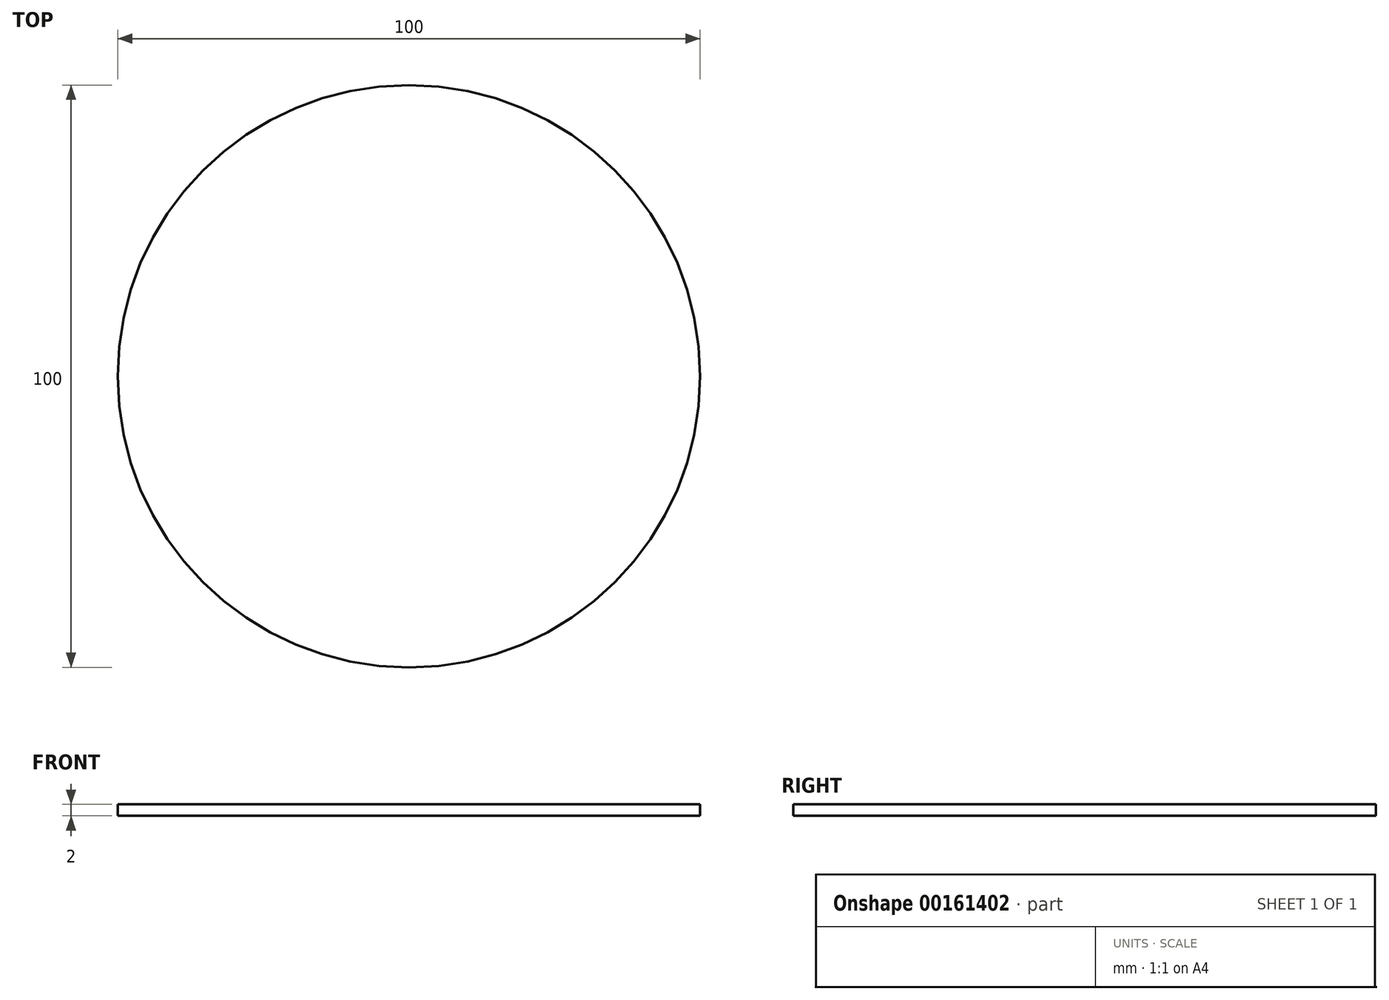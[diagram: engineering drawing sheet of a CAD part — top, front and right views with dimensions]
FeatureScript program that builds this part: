
annotation { "Feature Type Name" : "Feature", "Feature Type Description" : "" }
export const myFeature = defineFeature(function(context is Context, id is Id, definition is map)
    precondition{}
    {
        {
            var Q0;
            Q0=qCreatedBy(makeId("Top.planeOp"),FACE);
            var sketch = newSketch(context, id + "F1", { "sketchPlane" : qUnion([Q0])});
            skCircle(sketch, "E0", {"center": v(0, 0) * mm, "radius": 50 * mm});
            skSolve(sketch);
        }
        {
            var Q0;
            Q0=makeQuery(id+"F1.imprint","IMPRINT",FACE,{"disambiguationData":[TD([[makeQuery(id+"F1.imprint","IMPRINT",EDGE,{"derivedFrom":sQuery(id+"F1.wireOp",EDGE,"E0")}),1.0]])]});
            extrude(context, id + "F0", {"entities" : qUnion([Q0]), "depth" : 2 * mm});
        }
    });
